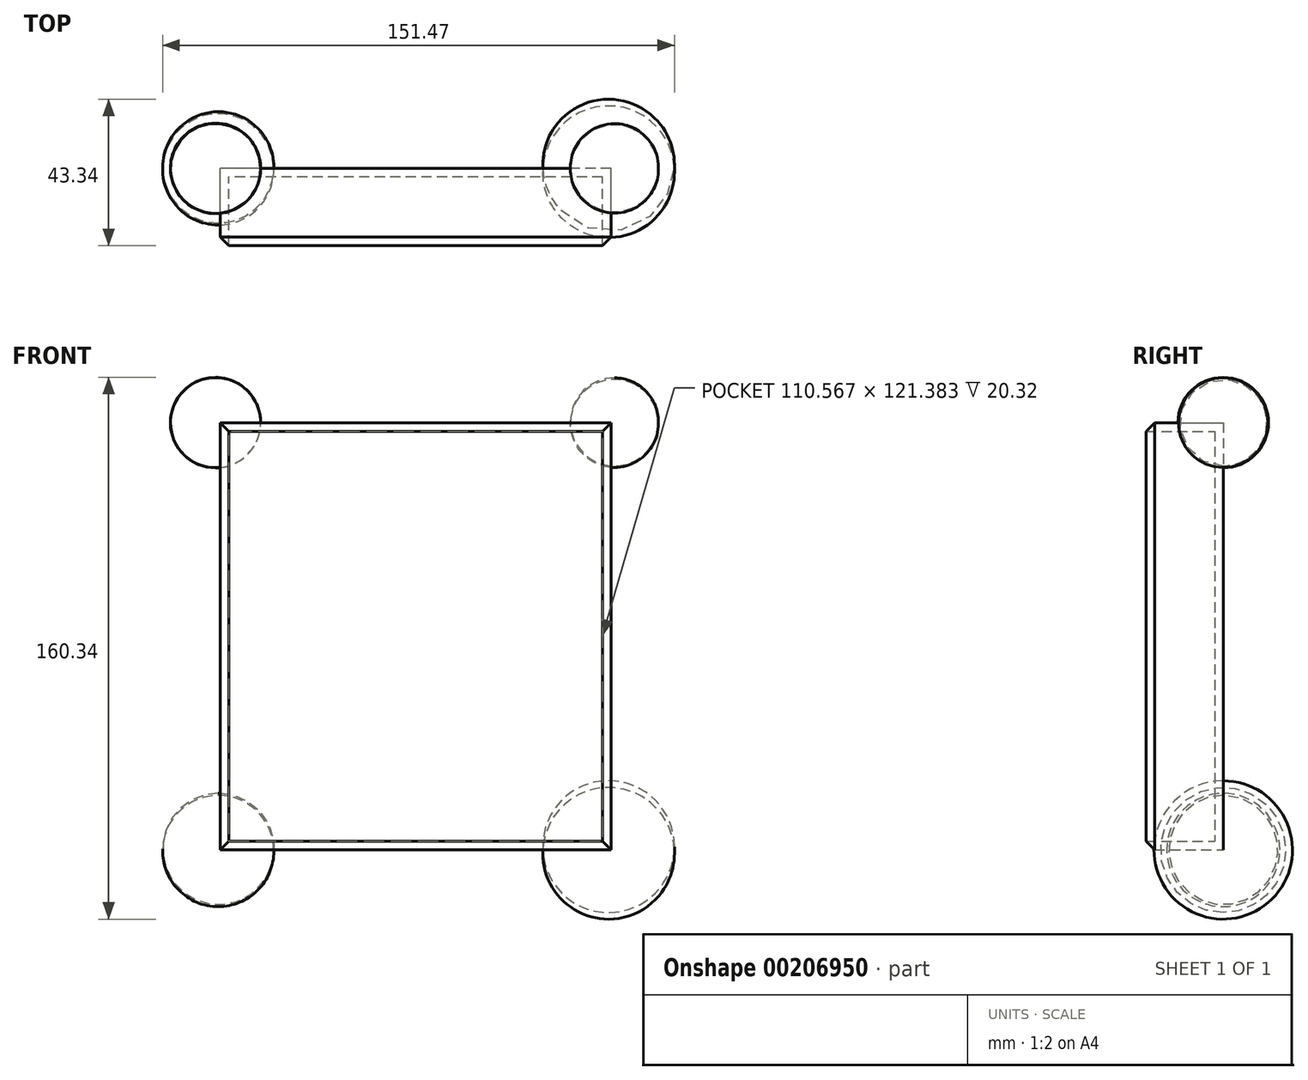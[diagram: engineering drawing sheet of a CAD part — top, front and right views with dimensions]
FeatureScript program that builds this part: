
annotation { "Feature Type Name" : "Feature", "Feature Type Description" : "" }
export const myFeature = defineFeature(function(context is Context, id is Id, definition is map)
    precondition{}
    {
        {
            var Q0;
            Q0=qCreatedBy(makeId("Front.planeOp"),FACE);
            var sketch = newSketch(context, id + "F0", { "sketchPlane" : qUnion([Q0])});
            skLineSegment(sketch, "E0.bottom", {"start": v(39.94, 50.34) * mm, "end": v(-75.71, 50.34) * mm});
            skLineSegment(sketch, "E0.top", {"start": v(39.94, -76.13) * mm, "end": v(-75.71, -76.13) * mm});
            skLineSegment(sketch, "E0.left", {"start": v(39.94, 50.34) * mm, "end": v(39.94, -76.13) * mm});
            skLineSegment(sketch, "E0.right", {"start": v(-75.71, 50.34) * mm, "end": v(-75.71, -76.13) * mm});
            skLineSegment(sketch, "E1", {"start": v(-63.76, 50.34) * mm, "end": v(-90.48, 50.34) * mm});
            skArc(sketch, "E2", {"start": v(-63.76, 50.34) * mm, "mid": v(-77.12, 63.73) * mm, "end": v(-90.48, 50.34) * mm});
            skLineSegment(sketch, "E3", {"start": v(27.93, 50.34) * mm, "end": v(53.99, 50.34) * mm});
            skArc(sketch, "E4", {"start": v(53.99, 50.34) * mm, "mid": v(40.96, 63.16) * mm, "end": v(27.93, 50.34) * mm});
            skLineSegment(sketch, "E5", {"start": v(-59.85, -76.13) * mm, "end": v(-92.76, -76.13) * mm});
            skLineSegment(sketch, "E6", {"start": v(19.74, -76.13) * mm, "end": v(58.69, -76.13) * mm});
            skArc(sketch, "E7", {"start": v(-92.76, -76.13) * mm, "mid": v(-76.3, -92.28) * mm, "end": v(-59.85, -76.13) * mm});
            skArc(sketch, "E8", {"start": v(19.74, -76.13) * mm, "mid": v(39.21, -94.64) * mm, "end": v(58.69, -76.13) * mm});
            skSolve(sketch);
        }
        {
            var Q0;
            {var subQ0=sQuery(id+"F0.wireOp",EDGE,"E2");Q0=makeQuery(id+"F0.imprint","IMPRINT",FACE,{"disambiguationData":[TD([[makeQuery(id+"F0.imprint","IMPRINT",EDGE,{"derivedFrom":subQ0}),1.0]])]});}
            var Q1;
            Q1=sQuery(id+"F0.wireOp",EDGE,"E1");
            revolve(context, id + "F1", {"entities" : qUnion([Q0]), "axis" : qUnion([Q1]), "revolveType" : RevolveType.FULL});
        }
        {
            var Q0;
            {var subQ0=sQuery(id+"F0.wireOp",EDGE,"E4");Q0=makeQuery(id+"F0.imprint","IMPRINT",FACE,{"disambiguationData":[TD([[makeQuery(id+"F0.imprint","IMPRINT",EDGE,{"derivedFrom":subQ0}),1.0]])]});}
            var Q1;
            Q1=sQuery(id+"F0.wireOp",EDGE,"E3");
            revolve(context, id + "F2", {"entities" : qUnion([Q0]), "axis" : qUnion([Q1]), "revolveType" : RevolveType.FULL});
        }
        {
            var Q0;
            {var subQ0=sQuery(id+"F0.wireOp",EDGE,"E7");Q0=makeQuery(id+"F0.imprint","IMPRINT",FACE,{"disambiguationData":[TD([[makeQuery(id+"F0.imprint","IMPRINT",EDGE,{"derivedFrom":subQ0}),1.0]])]});}
            var Q1;
            Q1=sQuery(id+"F0.wireOp",EDGE,"E5");
            revolve(context, id + "F3", {"entities" : qUnion([Q0]), "axis" : qUnion([Q1]), "revolveType" : RevolveType.FULL});
        }
        {
            var Q0;
            {var subQ0=sQuery(id+"F0.wireOp",EDGE,"E8");Q0=makeQuery(id+"F0.imprint","IMPRINT",FACE,{"disambiguationData":[TD([[makeQuery(id+"F0.imprint","IMPRINT",EDGE,{"derivedFrom":subQ0}),1.0]])]});}
            var Q1;
            Q1=sQuery(id+"F0.wireOp",EDGE,"E6");
            revolve(context, id + "F4", {"entities" : qUnion([Q0]), "axis" : qUnion([Q1]), "revolveType" : RevolveType.FULL});
        }
        {
            var Q0;
            {var subQ4=sQuery(id+"F0.wireOp",EDGE,"E0.bottom");Q0=makeQuery(id+"F0.imprint","IMPRINT",FACE,{"disambiguationData":[TD([[makeQuery(id+"F0.imprint","IMPRINT",EDGE,{"derivedFrom":subQ4}),1.0]])]});}
            extrude(context, id + "F5", {"entities" : qUnion([Q0]), "depth" : 25.4 * mm});
        }
        {
            var Q0;
            Q0=makeQuery(id+"F5.opExtrude","CAP_FACE",FACE,{"disambiguationData":[OSD([sQuery(id+"F0.wireOp",EDGE,"E0.bottom"),sQuery(id+"F0.wireOp",EDGE,"E0.top"),sQuery(id+"F0.wireOp",EDGE,"E0.left"),sQuery(id+"F0.wireOp",EDGE,"E0.right"),sQuery(id+"F0.wireOp",EDGE,"E1"),sQuery(id+"F0.wireOp",EDGE,"E3"),sQuery(id+"F0.wireOp",EDGE,"E5"),sQuery(id+"F0.wireOp",EDGE,"E6")])],"isStart":false});
            shell(context, id + "F6", {"entities" : qUnion([Q0]), "thickness" : 2.54 * mm});
        }
        {
            var Q0;
            Q0=makeQuery(id+"F5.opExtrude","CAP_EDGE",EDGE,{"disambiguationData":[OSD([sQuery(id+"F0.wireOp",EDGE,"E0.top"),sQuery(id+"F0.wireOp",EDGE,"E5"),sQuery(id+"F0.wireOp",EDGE,"E6")])],"isStart":false});
            var Q1;
            Q1=makeQuery(id+"F5.opExtrude","CAP_EDGE",EDGE,{"disambiguationData":[OSD([sQuery(id+"F0.wireOp",EDGE,"E0.left")])],"isStart":false});
            var Q2;
            Q2=makeQuery(id+"F5.opExtrude","CAP_EDGE",EDGE,{"disambiguationData":[OSD([sQuery(id+"F0.wireOp",EDGE,"E0.bottom"),sQuery(id+"F0.wireOp",EDGE,"E1"),sQuery(id+"F0.wireOp",EDGE,"E3")])],"isStart":false});
            var Q3;
            Q3=makeQuery(id+"F5.opExtrude","CAP_EDGE",EDGE,{"disambiguationData":[OSD([sQuery(id+"F0.wireOp",EDGE,"E0.right")])],"isStart":false});
            chamfer(context, id + "F7", {"entities" : qUnion([Q0, Q1, Q2, Q3]), "width" : 5.08 * mm, "tangentPropagation" : true});
        }
    });
